# Revit family: Sanitary_Showers_hansgrohe_26824XXX-Crometta-100-Hand-shower-Vario__1
name_source: partatom
category: Plumbing Fixtures
revit_build: Autodesk Revit 2018 (Build: 20170223_1515(x64)
units: mm (PartAtom-declared; Revit-internal decimal feet)

## family parameters
Always vertical = No
Cut with Voids When Loaded = No
OmniClass Number = 23.45.05.14.17
OmniClass Title = Showers
Part Type = Normal
Room Calculation Point = No
Round Connector Dimension = Use Diameter
Shared = No
Work Plane-Based = Yes

## types (1)
- 400 White/Chrome
    BIMobject category = Showers
    Default Elevation = 1219.2 mm  [stored 4 ft]
    Description = Crometta 100 Hand shower Vario
    Edition number = 1
    IFC Classification = Sanitary Terminal
    Manufacturer = Hansgrohe
    Manufacturer name = hansgrohe
    Masterformat 2014 Code = 22 41 23
    Masterformat 2014 Description = Residential Showers
    Material 1 = Hansgrohe - Metal - 000 Chrome
    Material 2 = Hansgrohe - Plastic - White
    Model = 26824XXX
    NBS Reference Code = 35-06-81
    NBS Reference Description = Shower Heads
    OmniClass Code = 23-31 17 19
    OmniClass Description = Shower Head Fixtures
    Product Guid = ac28f541-8bdc-4e65-a262-31bddeeeb2fa
    Product SKU = 26824XXX
    Product data url = https://bimobject.com
    Product family = Crometta 100
    Product group = Shower sets
    Product name = 26824XXX Crometta 100 Hand shower Vario
    QR code = https://www.bimobject.com
    UNSPSC Code = 30181503
    URL = https://www.hansgrohe.com
    Uniclass 2015 Code = Pr_40_20_87_76
    Uniclass 2015 Name = Shower heads
    Uniformat II Code = D2010
    Uniformat II Description = Plumbing Fixtures

note: [stored X ft] marks values corroborated as IEEE doubles in the binary element streams (Revit-internal decimal feet)

## geometry (parser evidence)
native form markers: Sweep x2
no freeform markers — native parametric forms only
